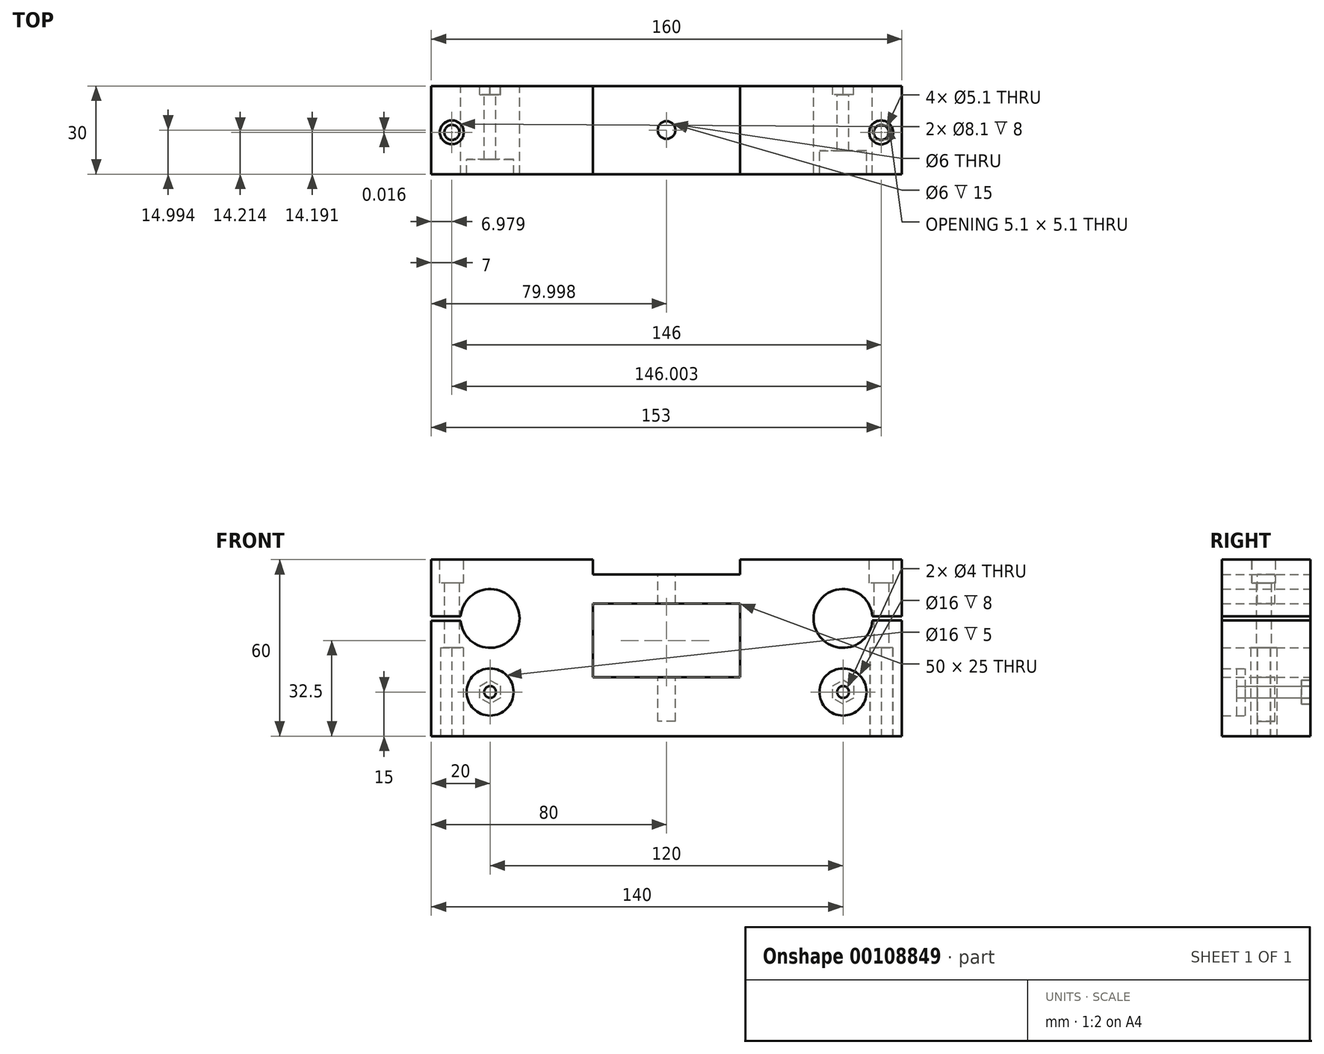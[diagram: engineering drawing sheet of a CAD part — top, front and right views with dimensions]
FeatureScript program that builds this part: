
annotation { "Feature Type Name" : "Feature", "Feature Type Description" : "" }
export const myFeature = defineFeature(function(context is Context, id is Id, definition is map)
    precondition{}
    {
        {
            var Q0;
            Q0=qCreatedBy(makeId("Front.planeOp"),FACE);
            var sketch = newSketch(context, id + "F0", { "sketchPlane" : qUnion([Q0])});
            skLineSegment(sketch, "E0.bottom", {"start": v(-20, 0) * mm, "end": v(140, 0) * mm});
            skLineSegment(sketch, "E0.top", {"start": v(-20, 60) * mm, "end": v(35, 60) * mm});
            skLineSegment(sketch, "E0.left", {"start": v(-20, 0) * mm, "end": v(-20, 39.23) * mm});
            skLineSegment(sketch, "E0.right", {"start": v(140, 0) * mm, "end": v(140, 39.3) * mm});
            skLineSegment(sketch, "E1", {"start": v(60, 68.67) * mm, "end": v(60, -11.64) * mm, "construction": true});
            skLineSegment(sketch, "E2", {"start": v(0, 64.15) * mm, "end": v(0, -12.13) * mm, "construction": true});
            skLineSegment(sketch, "E3", {"start": v(120, 65.28) * mm, "end": v(120, -11.74) * mm, "construction": true});
            skArc(sketch, "E4", {"start": v(-9.97, 39.23) * mm, "mid": v(10, 40.03) * mm, "end": v(-9.98, 40.7) * mm});
            skArc(sketch, "E5", {"start": v(129.98, 40.7) * mm, "mid": v(110, 40) * mm, "end": v(129.98, 39.3) * mm});
            skLineSegment(sketch, "E6", {"start": v(0, 50) * mm, "end": v(-26.2, 50) * mm, "construction": true});
            skLineSegment(sketch, "E7.top", {"start": v(-20, 40.7) * mm, "end": v(-9.98, 40.7) * mm});
            skLineSegment(sketch, "E8.top", {"start": v(-20, 39.23) * mm, "end": v(-9.97, 39.23) * mm});
            skLineSegment(sketch, "E9.top", {"start": v(140, 40.7) * mm, "end": v(129.98, 40.7) * mm});
            skLineSegment(sketch, "E10.top", {"start": v(140, 39.3) * mm, "end": v(129.98, 39.3) * mm});
            skLineSegment(sketch, "E11.bottom", {"start": v(35, 20) * mm, "end": v(85, 20) * mm});
            skLineSegment(sketch, "E11.top", {"start": v(35, 45) * mm, "end": v(85, 45) * mm});
            skLineSegment(sketch, "E11.left", {"start": v(35, 20) * mm, "end": v(35, 45) * mm});
            skLineSegment(sketch, "E11.right", {"start": v(85, 20) * mm, "end": v(85, 45) * mm});
            skLineSegment(sketch, "E12", {"start": v(35, 60) * mm, "end": v(35, 55) * mm});
            skLineSegment(sketch, "E13", {"start": v(85, 60) * mm, "end": v(85, 55) * mm});
            skLineSegment(sketch, "E14", {"start": v(35, 55) * mm, "end": v(85, 55) * mm});
            skLineSegment(sketch, "E15.trimOffspring", {"start": v(85, 60) * mm, "end": v(140, 60) * mm});
            skLineSegment(sketch, "E16.trimOffspring", {"start": v(2.06, 40) * mm, "end": v(125.05, 40) * mm, "construction": true});
            skLineSegment(sketch, "E17.trimOffspring", {"start": v(-20, 40.7) * mm, "end": v(-20, 60) * mm});
            skLineSegment(sketch, "E18.trimOffspring", {"start": v(140, 40.7) * mm, "end": v(140, 60) * mm});
            skLineSegment(sketch, "E19.trimOffspring", {"start": v(140, 40) * mm, "end": v(151.24, 40) * mm, "construction": true});
            skLineSegment(sketch, "E20", {"start": v(10, 40) * mm, "end": v(10, 13.45) * mm, "construction": true});
            skLineSegment(sketch, "E21", {"start": v(110, 40) * mm, "end": v(110, 11.67) * mm, "construction": true});
            skLineSegment(sketch, "E22", {"start": v(-28.32, 15) * mm, "end": v(153.8, 15) * mm, "construction": true});
            skPoint(sketch, "E23", {"position": v(0, 15) * mm});
            skPoint(sketch, "E24", {"position": v(120, 15) * mm});
            skCircle(sketch, "E25", {"center": v(0, 15) * mm, "radius": 8 * mm});
            skCircle(sketch, "E26", {"center": v(120, 15) * mm, "radius": 8 * mm});
            skCircle(sketch, "E27", {"center": v(0, 15) * mm, "radius": 2 * mm});
            skCircle(sketch, "E28", {"center": v(120, 15) * mm, "radius": 2 * mm});
            skCircle(sketch, "E29.cCircle", {"center": v(120, 15) * mm, "radius": 3.54 * mm, "construction": true});
            skLineSegment(sketch, "E29.0", {"start": v(116.46, 12.95) * mm, "end": v(116.46, 17.05) * mm});
            skLineSegment(sketch, "E29.1", {"start": v(116.46, 17.05) * mm, "end": v(120, 19.1) * mm});
            skLineSegment(sketch, "E29.2", {"start": v(120, 19.1) * mm, "end": v(123.54, 17.05) * mm});
            skLineSegment(sketch, "E29.3", {"start": v(123.54, 17.05) * mm, "end": v(123.54, 12.95) * mm});
            skLineSegment(sketch, "E29.4", {"start": v(123.54, 12.95) * mm, "end": v(120, 10.9) * mm});
            skLineSegment(sketch, "E29.5", {"start": v(120, 10.9) * mm, "end": v(116.46, 12.95) * mm});
            skPoint(sketch, "E29.0.midPoint", {"position": v(116.46, 15) * mm});
            skCircle(sketch, "E30.cCircle", {"center": v(0, 15) * mm, "radius": 3.5 * mm, "construction": true});
            skLineSegment(sketch, "E30.0", {"start": v(-3.52, 16.98) * mm, "end": v(-0.04, 19.04) * mm});
            skLineSegment(sketch, "E30.1", {"start": v(-0.04, 19.04) * mm, "end": v(3.48, 17.06) * mm});
            skLineSegment(sketch, "E30.2", {"start": v(3.48, 17.06) * mm, "end": v(3.52, 13.02) * mm});
            skLineSegment(sketch, "E30.3", {"start": v(3.52, 13.02) * mm, "end": v(0.04, 10.96) * mm});
            skLineSegment(sketch, "E30.4", {"start": v(0.04, 10.96) * mm, "end": v(-3.48, 12.94) * mm});
            skLineSegment(sketch, "E30.5", {"start": v(-3.48, 12.94) * mm, "end": v(-3.52, 16.98) * mm});
            skPoint(sketch, "E30.0.midPoint", {"position": v(-1.78, 18.01) * mm});
            skSolve(sketch);
        }
        {
            var Q0;
            Q0=makeQuery(id+"F0.imprint","IMPRINT",FACE,{"disambiguationData":[TD([[makeQuery(id+"F0.imprint","IMPRINT",EDGE,{"derivedFrom":sQuery(id+"F0.wireOp",EDGE,"E0.bottom")}),1.0]])]});
            var Q1;
            Q1=makeQuery(id+"F0.imprint","IMPRINT",FACE,{"disambiguationData":[TD([[makeQuery(id+"F0.imprint","IMPRINT",EDGE,{"derivedFrom":sQuery(id+"F0.wireOp",EDGE,"E27")}),-1.0]])]});
            var Q2;
            Q2=makeQuery(id+"F0.imprint","IMPRINT",FACE,{"disambiguationData":[TD([[makeQuery(id+"F0.imprint","IMPRINT",EDGE,{"derivedFrom":sQuery(id+"F0.wireOp",EDGE,"E28")}),-1.0]])]});
            extrude(context, id + "F1", {"entities" : qUnion([Q0, Q1, Q2]), "depth" : 30 * mm});
        }
        {
            var Q0;
            Q0=qCreatedBy(makeId("Top.planeOp"),FACE);
            var sketch = newSketch(context, id + "F2", { "sketchPlane" : qUnion([Q0])});
            skLineSegment(sketch, "E31", {"start": v(38, 0) * mm, "end": v(38, -38.86) * mm, "construction": true});
            skLineSegment(sketch, "E32", {"start": v(88, 0) * mm, "end": v(88, -38.12) * mm, "construction": true});
            skLineSegment(sketch, "E33", {"start": v(-24.4, 0) * mm, "end": v(144.16, 0) * mm});
            skLineSegment(sketch, "E34", {"start": v(-13, 7.6) * mm, "end": v(-13, -37.06) * mm, "construction": true});
            skLineSegment(sketch, "E35", {"start": v(133, 6.36) * mm, "end": v(133, -40.54) * mm, "construction": true});
            skLineSegment(sketch, "E36", {"start": v(-28.81, -15.8) * mm, "end": v(140.25, -15.8) * mm, "construction": true});
            skLineSegment(sketch, "E37", {"start": v(138, 0) * mm, "end": v(138, -40.8) * mm, "construction": true});
            skCircle(sketch, "E38", {"center": v(133, -15.8) * mm, "radius": 2.55 * mm});
            skCircle(sketch, "E39", {"center": v(-13, -15.8) * mm, "radius": 2.55 * mm});
            skLineSegment(sketch, "E40.0", {"start": v(-16.85, -18.04) * mm, "end": v(-16.86, -13.6) * mm});
            skLineSegment(sketch, "E40.1", {"start": v(-16.86, -13.6) * mm, "end": v(-13.01, -11.36) * mm});
            skLineSegment(sketch, "E40.2", {"start": v(-13.01, -11.36) * mm, "end": v(-9.15, -13.57) * mm});
            skLineSegment(sketch, "E40.3", {"start": v(-9.15, -13.57) * mm, "end": v(-9.14, -18.02) * mm});
            skLineSegment(sketch, "E40.4", {"start": v(-9.14, -18.02) * mm, "end": v(-12.99, -20.26) * mm});
            skLineSegment(sketch, "E40.5", {"start": v(-12.99, -20.26) * mm, "end": v(-16.85, -18.04) * mm});
            skCircle(sketch, "E41.cCircle", {"center": v(133, -15.8) * mm, "radius": 4.45 * mm, "construction": true});
            skLineSegment(sketch, "E41.0", {"start": v(129.12, -17.99) * mm, "end": v(129.17, -13.54) * mm});
            skLineSegment(sketch, "E41.1", {"start": v(129.17, -13.54) * mm, "end": v(133.05, -11.36) * mm});
            skLineSegment(sketch, "E41.2", {"start": v(133.05, -11.36) * mm, "end": v(136.88, -13.63) * mm});
            skLineSegment(sketch, "E41.3", {"start": v(136.88, -13.63) * mm, "end": v(136.83, -18.08) * mm});
            skLineSegment(sketch, "E41.4", {"start": v(136.83, -18.08) * mm, "end": v(132.95, -20.26) * mm});
            skLineSegment(sketch, "E41.5", {"start": v(132.95, -20.26) * mm, "end": v(129.12, -17.99) * mm});
            skLineSegment(sketch, "E42", {"start": v(-13, -30.07) * mm, "end": v(-13, -34.76) * mm, "construction": true});
            skLineSegment(sketch, "E43", {"start": v(-12.99, -20.26) * mm, "end": v(-13.01, -11.36) * mm, "construction": true});
            skSolve(sketch);
        }
        {
            var Q0;
            Q0=makeQuery(id+"F2.imprint","IMPRINT",FACE,{"disambiguationData":[TD([[makeQuery(id+"F2.imprint","IMPRINT",EDGE,{"derivedFrom":sQuery(id+"F2.wireOp",EDGE,"E39")}),1.0]])]});
            var Q1;
            Q1=makeQuery(id+"F2.imprint","IMPRINT",FACE,{"disambiguationData":[TD([[makeQuery(id+"F2.imprint","IMPRINT",EDGE,{"derivedFrom":sQuery(id+"F2.wireOp",EDGE,"E38")}),1.0]])]});
            extrude(context, id + "F3", {"entities" : qUnion([Q0, Q1]), "operationType" : NewBodyOperationType.REMOVE, "depth" : 60 * mm});
        }
        {
            var Q0;
            Q0=qCreatedBy(makeId("Top.planeOp"),FACE);
            var sketch = newSketch(context, id + "F4", { "sketchPlane" : qUnion([Q0])});
            skLineSegment(sketch, "E44", {"start": v(-25.12, -15) * mm, "end": v(138.46, -15) * mm, "construction": true});
            skLineSegment(sketch, "E45", {"start": v(-24.91, -2.15) * mm, "end": v(-24.91, 28.18) * mm, "construction": true});
            skLineSegment(sketch, "E46", {"start": v(125.09, -10.34) * mm, "end": v(125.09, 29.3) * mm, "construction": true});
            skLineSegment(sketch, "E47", {"start": v(60, 30.23) * mm, "end": v(60, -44.58) * mm, "construction": true});
            skLineSegment(sketch, "E48", {"start": v(150.99, 0) * mm, "end": v(0, 0) * mm, "construction": true});
            skLineSegment(sketch, "E49", {"start": v(126.91, -30) * mm, "end": v(156.63, -30) * mm, "construction": true});
            skCircle(sketch, "E50", {"center": v(60, -15) * mm, "radius": 3.02 * mm});
            skSolve(sketch);
        }
        {
            var Q0;
            Q0=makeQuery(id+"F2.imprint","IMPRINT",FACE,{"disambiguationData":[TD([[makeQuery(id+"F2.imprint","IMPRINT",EDGE,{"derivedFrom":sQuery(id+"F2.wireOp",EDGE,"E39")}),-1.0]])]});
            var Q1;
            Q1=makeQuery(id+"F2.imprint","IMPRINT",FACE,{"disambiguationData":[TD([[makeQuery(id+"F2.imprint","IMPRINT",EDGE,{"derivedFrom":sQuery(id+"F2.wireOp",EDGE,"E38")}),-1.0]])]});
            extrude(context, id + "F5", {"entities" : qUnion([Q0, Q1]), "operationType" : NewBodyOperationType.REMOVE, "depth" : 30 * mm});
        }
        {
            var Q0;
            Q0=qCreatedBy(makeId("Top.planeOp"),FACE);
            var sketch = newSketch(context, id + "F6", { "sketchPlane" : qUnion([Q0])});
            skCircle(sketch, "E51", {"center": v(-13, -15.8) * mm, "radius": 4.84 * mm});
            skCircle(sketch, "E52", {"center": v(133, -15.8) * mm, "radius": 4.05 * mm});
            skLineSegment(sketch, "E53", {"start": v(-21, 0) * mm, "end": v(-21, 5.23) * mm, "construction": true});
            skLineSegment(sketch, "E54", {"start": v(140, 0) * mm, "end": v(140, 16.2) * mm, "construction": true});
            skSolve(sketch);
        }
        {
            var Q0;
            Q0=makeQuery(id+"F6.imprint","IMPRINT",FACE,{"disambiguationData":[TD([[makeQuery(id+"F6.imprint","IMPRINT",EDGE,{"derivedFrom":sQuery(id+"F6.wireOp",EDGE,"E51")}),1.0]])]});
            var Q1;
            Q1=makeQuery(id+"F6.imprint","IMPRINT",FACE,{"disambiguationData":[TD([[makeQuery(id+"F6.imprint","IMPRINT",EDGE,{"derivedFrom":sQuery(id+"F6.wireOp",EDGE,"E52")}),1.0]])]});
            extrude(context, id + "F7", {"entities" : qUnion([Q0, Q1]), "operationType" : NewBodyOperationType.REMOVE, "oppositeDirection" : true, "depth" : 8 * mm});
        }
        {
            var Q0;
            Q0=makeQuery(id+"F4.imprint","IMPRINT",FACE,{"disambiguationData":[TD([[makeQuery(id+"F4.imprint","IMPRINT",EDGE,{"derivedFrom":sQuery(id+"F4.wireOp",EDGE,"E50")}),1.0]])]});
            var Q1;
            Q1=sQuery(id+"F4.wireOp",EDGE,"E50");
            extrude(context, id + "F8", {"entities" : qUnion([Q0]), "operationType" : NewBodyOperationType.REMOVE, "surfaceEntities" : qUnion([Q1]), "oppositeDirection" : true, "depth" : 55 * mm});
        }
        {
            var Q0;
            Q0=makeQuery(id+"F0.imprint","IMPRINT",FACE,{"disambiguationData":[TD([[makeQuery(id+"F0.imprint","IMPRINT",EDGE,{"derivedFrom":sQuery(id+"F0.wireOp",EDGE,"E25")}),1.0]])]});
            var Q1;
            Q1=makeQuery(id+"F0.imprint","IMPRINT",FACE,{"disambiguationData":[TD([[makeQuery(id+"F0.imprint","IMPRINT",EDGE,{"derivedFrom":sQuery(id+"F0.wireOp",EDGE,"E26")}),1.0]])]});
            extrude(context, id + "F9", {"entities" : qUnion([Q0, Q1]), "operationType" : NewBodyOperationType.ADD, "depth" : 22 * mm});
        }
        {
            var Q0;
            Q0=makeQuery(id+"F0.imprint","IMPRINT",FACE,{"disambiguationData":[TD([[makeQuery(id+"F0.imprint","IMPRINT",EDGE,{"derivedFrom":sQuery(id+"F0.wireOp",EDGE,"E28")}),-1.0]])]});
            extrude(context, id + "F10", {"entities" : qUnion([Q0]), "operationType" : NewBodyOperationType.REMOVE, "oppositeDirection" : true, "depth" : 4 * mm});
        }
        {
            var Q0;
            Q0=makeQuery(id+"F0.imprint","IMPRINT",FACE,{"disambiguationData":[TD([[makeQuery(id+"F0.imprint","IMPRINT",EDGE,{"derivedFrom":sQuery(id+"F0.wireOp",EDGE,"E28")}),-1.0]])]});
            extrude(context, id + "F11", {"entities" : qUnion([Q0]), "operationType" : NewBodyOperationType.REMOVE, "oppositeDirection" : true, "depth" : 3 * mm});
        }
        {
            var Q0;
            Q0=makeQuery(id+"F0.imprint","IMPRINT",FACE,{"disambiguationData":[TD([[makeQuery(id+"F0.imprint","IMPRINT",EDGE,{"derivedFrom":sQuery(id+"F0.wireOp",EDGE,"E28")}),-1.0]])]});
            extrude(context, id + "F12", {"entities" : qUnion([Q0]), "operationType" : NewBodyOperationType.REMOVE, "depth" : 3 * mm});
        }
        {
            var Q0;
            Q0=makeQuery(id+"F0.imprint","IMPRINT",FACE,{"disambiguationData":[TD([[makeQuery(id+"F0.imprint","IMPRINT",EDGE,{"derivedFrom":sQuery(id+"F0.wireOp",EDGE,"E27")}),-1.0]])]});
            extrude(context, id + "F13", {"entities" : qUnion([Q0]), "operationType" : NewBodyOperationType.REMOVE, "depth" : 3 * mm});
        }
        {
            var Q0;
            Q0=makeQuery(id+"F0.imprint","IMPRINT",FACE,{"disambiguationData":[TD([[makeQuery(id+"F0.imprint","IMPRINT",EDGE,{"derivedFrom":sQuery(id+"F0.wireOp",EDGE,"E25")}),1.0]])]});
            extrude(context, id + "F14", {"entities" : qUnion([Q0]), "operationType" : NewBodyOperationType.ADD, "depth" : 25 * mm});
        }
        {
            var Q0;
            Q0=makeQuery(id+"F1.opExtrude","CAP_FACE",FACE,{"disambiguationData":[OSD([sQuery(id+"F0.wireOp",EDGE,"E27"),sQuery(id+"F0.wireOp",EDGE,"E30.0"),sQuery(id+"F0.wireOp",EDGE,"E30.1"),sQuery(id+"F0.wireOp",EDGE,"E30.2"),sQuery(id+"F0.wireOp",EDGE,"E30.3"),sQuery(id+"F0.wireOp",EDGE,"E30.4"),sQuery(id+"F0.wireOp",EDGE,"E30.5")])],"isStart":false});
            extrude(context, id + "F15", {"entities" : qUnion([Q0]), "operationType" : NewBodyOperationType.REMOVE, "oppositeDirection" : true, "depth" : 5 * mm});
        }
        {
            var Q0;
            Q0=makeQuery(id+"F1.opExtrude","CAP_FACE",FACE,{"disambiguationData":[OSD([sQuery(id+"F0.wireOp",EDGE,"E28"),sQuery(id+"F0.wireOp",EDGE,"E29.0"),sQuery(id+"F0.wireOp",EDGE,"E29.1"),sQuery(id+"F0.wireOp",EDGE,"E29.2"),sQuery(id+"F0.wireOp",EDGE,"E29.3"),sQuery(id+"F0.wireOp",EDGE,"E29.4"),sQuery(id+"F0.wireOp",EDGE,"E29.5")])],"isStart":false});
            extrude(context, id + "F16", {"entities" : qUnion([Q0]), "operationType" : NewBodyOperationType.REMOVE, "oppositeDirection" : true, "depth" : 14.25 * mm});
        }
        {
            var Q0;
            Q0=makeQuery(id+"F16.boolean.opBoolean","COPY",FACE,{"derivedFrom":makeQuery(id+"F16.opExtrude","CAP_FACE",FACE,{"disambiguationData":[OSD([sQuery(id+"F0.wireOp",EDGE,"E28"),sQuery(id+"F0.wireOp",EDGE,"E29.0"),sQuery(id+"F0.wireOp",EDGE,"E29.1"),sQuery(id+"F0.wireOp",EDGE,"E29.2"),sQuery(id+"F0.wireOp",EDGE,"E29.3"),sQuery(id+"F0.wireOp",EDGE,"E29.4"),sQuery(id+"F0.wireOp",EDGE,"E29.5")])],"isStart":false})});
            var Q1;
            Q1=makeQuery(id+"F9.opExtrude","CAP_FACE",FACE,{"disambiguationData":[OSD([sQuery(id+"F0.wireOp",EDGE,"E26"),sQuery(id+"F0.wireOp",EDGE,"E29.0"),sQuery(id+"F0.wireOp",EDGE,"E29.1"),sQuery(id+"F0.wireOp",EDGE,"E29.2"),sQuery(id+"F0.wireOp",EDGE,"E29.3"),sQuery(id+"F0.wireOp",EDGE,"E29.4"),sQuery(id+"F0.wireOp",EDGE,"E29.5")])],"isStart":false});
            extrude(context, id + "F17", {"entities" : qUnion([Q0]), "operationType" : NewBodyOperationType.ADD, "endBound" : BoundingType.UP_TO_SURFACE, "endBoundEntityFace" : qUnion([Q1]), "depth" : 6.37 * mm});
        }
        {
            var Q0;
            Q0=makeQuery(id+"F1.opExtrude","SWEPT_FACE",FACE,{"disambiguationData":[OSD([sQuery(id+"F0.wireOp",EDGE,"E14")])]});
            cPlane(context, id + "F18", {"entities" : qUnion([Q0]), "cplaneType" : CPlaneType.OFFSET, "offset" : 0 * mm, "width" : 150 * mm, "height" : 150 * mm});
        }
        {
            var Q0;
            Q0=qCreatedBy(id+"F18.planeOp",FACE);
            var sketch = newSketch(context, id + "F19", { "sketchPlane" : qUnion([Q0])});
            skCircle(sketch, "E55", {"center": v(60, -15) * mm, "radius": 3 * mm});
            skSolve(sketch);
        }
        {
            var Q0;
            Q0=makeQuery(id+"F19.imprint","IMPRINT",FACE,{"disambiguationData":[TD([[makeQuery(id+"F19.imprint","IMPRINT",EDGE,{"derivedFrom":sQuery(id+"F19.wireOp",EDGE,"E55")}),1.0]])]});
            extrude(context, id + "F20", {"entities" : qUnion([Q0]), "operationType" : NewBodyOperationType.REMOVE, "oppositeDirection" : true, "depth" : 50 * mm});
        }
        {
            var Q0;
            Q0=makeQuery(id+"F1.opExtrude","SWEPT_FACE",FACE,{"disambiguationData":[OSD([sQuery(id+"F0.wireOp",EDGE,"E15.trimOffspring")])]});
            cPlane(context, id + "F21", {"entities" : qUnion([Q0]), "cplaneType" : CPlaneType.OFFSET, "offset" : 0 * mm, "width" : 150 * mm, "height" : 150 * mm});
        }
        {
            var Q0;
            Q0=qCreatedBy(id+"F21.planeOp",FACE);
            var sketch = newSketch(context, id + "F22", { "sketchPlane" : qUnion([Q0])});
            skCircle(sketch, "E56", {"center": v(-13.02, -15.77) * mm, "radius": 4.05 * mm});
            skCircle(sketch, "E57", {"center": v(132.98, -15.79) * mm, "radius": 4.05 * mm});
            skSolve(sketch);
        }
        {
            var Q0;
            Q0=makeQuery(id+"F22.imprint","IMPRINT",FACE,{"disambiguationData":[TD([[makeQuery(id+"F22.imprint","IMPRINT",EDGE,{"derivedFrom":sQuery(id+"F22.wireOp",EDGE,"E56")}),1.0]])]});
            var Q1;
            Q1=makeQuery(id+"F22.imprint","IMPRINT",FACE,{"disambiguationData":[TD([[makeQuery(id+"F22.imprint","IMPRINT",EDGE,{"derivedFrom":sQuery(id+"F22.wireOp",EDGE,"E57")}),1.0]])]});
            extrude(context, id + "F23", {"entities" : qUnion([Q0, Q1]), "operationType" : NewBodyOperationType.REMOVE, "oppositeDirection" : true, "depth" : 8 * mm});
        }
    });
